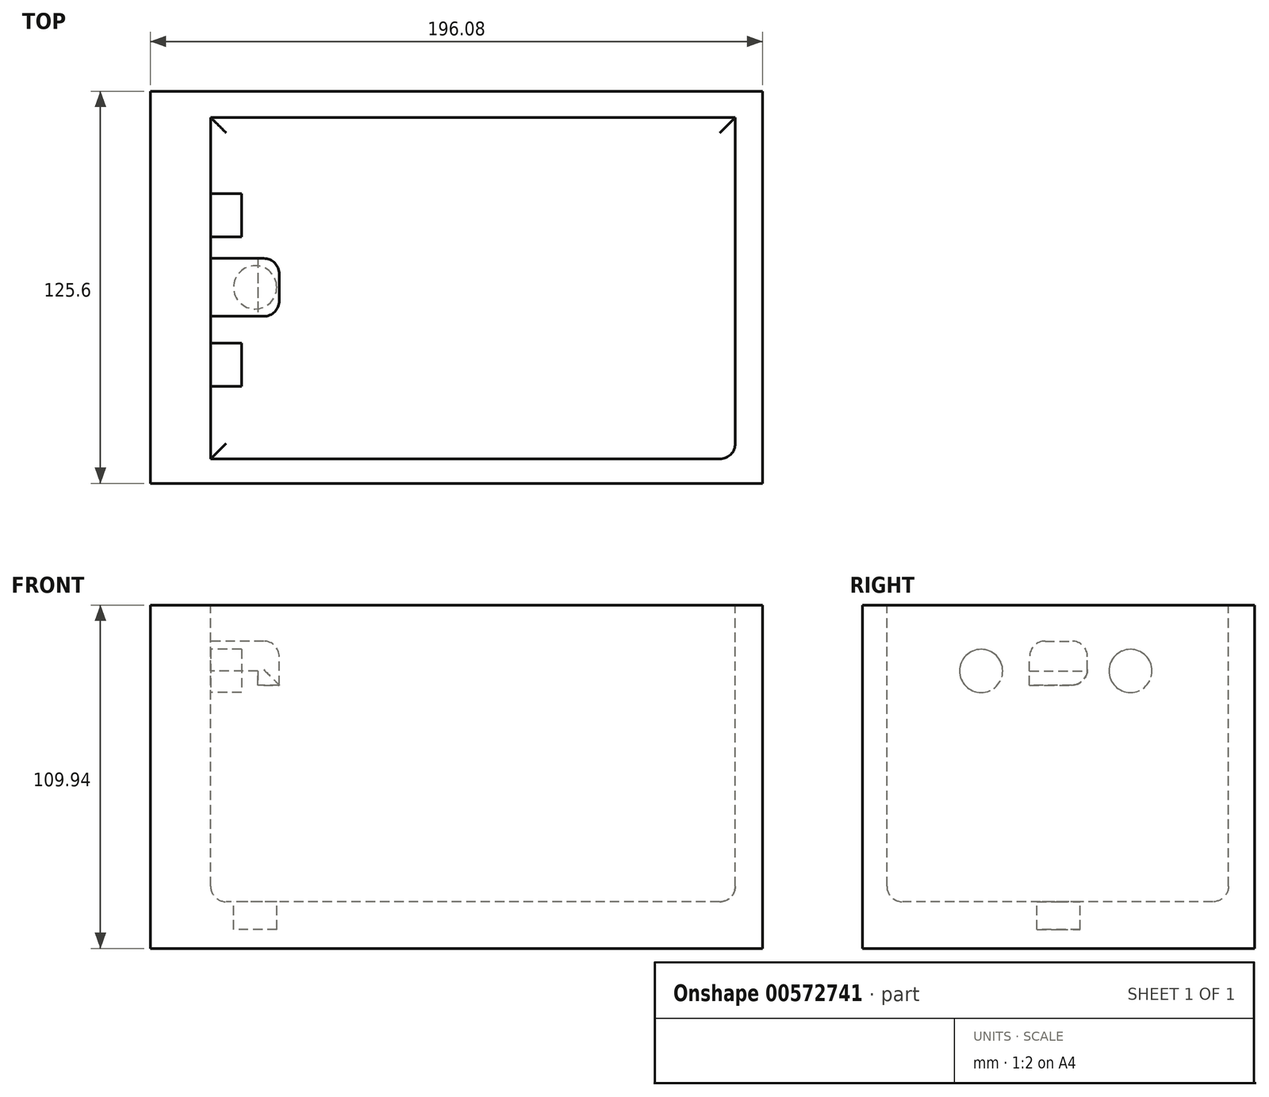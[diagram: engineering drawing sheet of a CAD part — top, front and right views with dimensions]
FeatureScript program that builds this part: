
annotation { "Feature Type Name" : "Feature", "Feature Type Description" : "" }
export const myFeature = defineFeature(function(context is Context, id is Id, definition is map)
    precondition{}
    {
        {
            var Q0;
            Q0=qCreatedBy(makeId("Front.planeOp"),FACE);
            var sketch = newSketch(context, id + "F0", { "sketchPlane" : qUnion([Q0])});
            skLineSegment(sketch, "E0.bottom", {"start": v(98.04, 54.97) * mm, "end": v(-98.04, 54.97) * mm});
            skLineSegment(sketch, "E0.top", {"start": v(98.04, -54.97) * mm, "end": v(-98.04, -54.97) * mm});
            skLineSegment(sketch, "E0.left", {"start": v(98.04, 54.97) * mm, "end": v(98.04, -54.97) * mm});
            skLineSegment(sketch, "E0.right", {"start": v(-98.04, 54.97) * mm, "end": v(-98.04, -54.97) * mm});
            skPoint(sketch, "E0.middle", {"position": v(0, 0) * mm});
            skSolve(sketch);
        }
        {
            var Q0;
            Q0=makeQuery(id+"F0.imprint","IMPRINT",FACE,{"disambiguationData":[TD([[makeQuery(id+"F0.imprint","IMPRINT",EDGE,{"derivedFrom":sQuery(id+"F0.wireOp",EDGE,"E0.bottom")}),1.0]])]});
            extrude(context, id + "F1", {"entities" : qUnion([Q0]), "endBound" : BoundingType.SYMMETRIC, "depth" : 125.6 * mm, "offsetDistance" : 25 * mm});
        }
        {
            var Q0;
            Q0=makeQuery(id+"F1.opExtrude","SWEPT_FACE",FACE,{"disambiguationData":[OSD([sQuery(id+"F0.wireOp",EDGE,"E0.bottom")])]});
            var sketch = newSketch(context, id + "F2", { "sketchPlane" : qUnion([Q0])});
            skLineSegment(sketch, "E1.bottom", {"start": v(89.32, 54.44) * mm, "end": v(-78.75, 54.44) * mm});
            skLineSegment(sketch, "E1.top", {"start": v(89.32, -54.97) * mm, "end": v(-78.75, -54.97) * mm});
            skLineSegment(sketch, "E1.left", {"start": v(89.32, 54.44) * mm, "end": v(89.32, -54.97) * mm});
            skLineSegment(sketch, "E1.right", {"start": v(-78.75, 54.44) * mm, "end": v(-78.75, -54.97) * mm});
            skSolve(sketch);
        }
        {
            var Q0;
            Q0=makeQuery(id+"F2.imprint","IMPRINT",FACE,{"disambiguationData":[TD([[makeQuery(id+"F2.imprint","IMPRINT",EDGE,{"derivedFrom":sQuery(id+"F2.wireOp",EDGE,"E1.bottom")}),1.0]])]});
            extrude(context, id + "F3", {"entities" : qUnion([Q0]), "operationType" : NewBodyOperationType.REMOVE, "oppositeDirection" : true, "depth" : 95 * mm, "offsetDistance" : 25 * mm});
        }
        {
            var Q0;
            Q0=makeQuery(id+"F3.boolean.opBoolean","COPY",FACE,{"derivedFrom":makeQuery(id+"F3.opExtrude","CAP_FACE",FACE,{"disambiguationData":[OSD([sQuery(id+"F2.wireOp",EDGE,"E1.bottom"),sQuery(id+"F2.wireOp",EDGE,"E1.top"),sQuery(id+"F2.wireOp",EDGE,"E1.left"),sQuery(id+"F2.wireOp",EDGE,"E1.right")])],"isStart":false})});
            var sketch = newSketch(context, id + "F4", { "sketchPlane" : qUnion([Q0])});
            skCircle(sketch, "E2", {"center": v(-64.48, 0) * mm, "radius": 6.92 * mm});
            skSolve(sketch);
        }
        {
            var Q0;
            Q0=makeQuery(id+"F4.imprint","IMPRINT",FACE,{"disambiguationData":[TD([[makeQuery(id+"F4.imprint","IMPRINT",EDGE,{"derivedFrom":sQuery(id+"F4.wireOp",EDGE,"E2")}),1.0]])]});
            extrude(context, id + "F5", {"entities" : qUnion([Q0]), "operationType" : NewBodyOperationType.REMOVE, "oppositeDirection" : true, "depth" : 8.9 * mm, "offsetDistance" : 25 * mm});
        }
        {
            var Q0;
            Q0=makeQuery(id+"F3.boolean.opBoolean","COPY",FACE,{"derivedFrom":makeQuery(id+"F3.opExtrude","SWEPT_FACE",FACE,{"disambiguationData":[OSD([sQuery(id+"F2.wireOp",EDGE,"E1.right")])]})});
            var sketch = newSketch(context, id + "F6", { "sketchPlane" : qUnion([Q0])});
            skLineSegment(sketch, "E3.bottom", {"start": v(-9.27, 33.92) * mm, "end": v(9.27, 33.92) * mm});
            skLineSegment(sketch, "E3.top", {"start": v(-9.27, 43.45) * mm, "end": v(9.27, 43.45) * mm});
            skLineSegment(sketch, "E3.left", {"start": v(-9.27, 33.92) * mm, "end": v(-9.27, 43.45) * mm});
            skLineSegment(sketch, "E3.right", {"start": v(9.27, 33.92) * mm, "end": v(9.27, 43.45) * mm});
            skPoint(sketch, "E3.middle", {"position": v(0, 38.69) * mm});
            skSolve(sketch);
        }
        {
            var Q0;
            Q0=makeQuery(id+"F6.imprint","IMPRINT",FACE,{"disambiguationData":[TD([[makeQuery(id+"F6.imprint","IMPRINT",EDGE,{"derivedFrom":sQuery(id+"F6.wireOp",EDGE,"E3.bottom")}),1.0]])]});
            extrude(context, id + "F7", {"entities" : qUnion([Q0]), "operationType" : NewBodyOperationType.ADD, "depth" : 22 * mm, "offsetDistance" : 25 * mm});
        }
        {
            var Q0;
            Q0=makeQuery(id+"F7.opExtrude","SWEPT_FACE",FACE,{"disambiguationData":[OSD([sQuery(id+"F6.wireOp",EDGE,"E3.top")])]});
            var sketch = newSketch(context, id + "F8", { "sketchPlane" : qUnion([Q0])});
            skLineSegment(sketch, "E4.bottom", {"start": v(-56.75, 9.27) * mm, "end": v(-63.69, 9.27) * mm});
            skLineSegment(sketch, "E4.top", {"start": v(-56.75, -9.27) * mm, "end": v(-63.69, -9.27) * mm});
            skLineSegment(sketch, "E4.left", {"start": v(-56.75, 9.27) * mm, "end": v(-56.75, -9.27) * mm});
            skLineSegment(sketch, "E4.right", {"start": v(-63.69, 9.27) * mm, "end": v(-63.69, -9.27) * mm});
            skSolve(sketch);
        }
        {
            var Q0;
            Q0=makeQuery(id+"F8.imprint","IMPRINT",FACE,{"disambiguationData":[TD([[makeQuery(id+"F8.imprint","IMPRINT",EDGE,{"derivedFrom":sQuery(id+"F8.wireOp",EDGE,"E4.bottom")}),1.0]])]});
            extrude(context, id + "F9", {"entities" : qUnion([Q0]), "operationType" : NewBodyOperationType.ADD, "oppositeDirection" : true, "depth" : 14.1 * mm, "offsetDistance" : 25 * mm});
        }
        {
            var Q0;
            Q0=makeQuery(id+"F3.boolean.opBoolean","COPY",EDGE,{"derivedFrom":makeQuery(id+"F3.opExtrude","CAP_EDGE",EDGE,{"disambiguationData":[OSD([sQuery(id+"F2.wireOp",EDGE,"E1.top")])],"isStart":true})});
            var Q1;
            Q1=makeQuery(id+"F3.boolean.opBoolean","COPY",EDGE,{"derivedFrom":makeQuery(id+"F3.opExtrude","SWEPT_EDGE",EDGE,{"disambiguationData":[OSD([sQuery(id+"F2.wireOp",EDGE,"E1.top"),sQuery(id+"F2.wireOp",EDGE,"E1.left")])]})});
            var Q2;
            Q2=makeQuery(id+"F3.boolean.opBoolean","COPY",EDGE,{"derivedFrom":makeQuery(id+"F3.opExtrude","CAP_EDGE",EDGE,{"disambiguationData":[OSD([sQuery(id+"F2.wireOp",EDGE,"E1.top")])],"isStart":false})});
            var Q3;
            Q3=makeQuery(id+"F7.opExtrude","SWEPT_EDGE",EDGE,{"disambiguationData":[OSD([sQuery(id+"F6.wireOp",EDGE,"E3.top"),sQuery(id+"F6.wireOp",EDGE,"E3.right")])]});
            var Q4;
            Q4=makeQuery(id+"F7.opExtrude","SWEPT_EDGE",EDGE,{"disambiguationData":[OSD([sQuery(id+"F6.wireOp",EDGE,"E3.top"),sQuery(id+"F6.wireOp",EDGE,"E3.left")])]});
            var Q5;
            Q5=makeQuery(id+"F7.opExtrude","CAP_EDGE",EDGE,{"disambiguationData":[OSD([sQuery(id+"F6.wireOp",EDGE,"E3.top")])],"isStart":false});
            var Q6;
            Q6=makeQuery(id+"F9.opExtrude","CAP_EDGE",EDGE,{"disambiguationData":[OSD([sQuery(id+"F8.wireOp",EDGE,"E4.bottom")])],"isStart":false});
            var Q7;
            Q7=makeQuery(id+"F9.boolean.opBoolean","MERGE",EDGE,{"derivedFrom":[makeQuery(id+"F7.opExtrude","CAP_EDGE",EDGE,{"disambiguationData":[OSD([sQuery(id+"F6.wireOp",EDGE,"E3.left")])],"isStart":false}),makeQuery(id+"F9.opExtrude","SWEPT_EDGE",EDGE,{"disambiguationData":[OSD([sQuery(id+"F8.wireOp",EDGE,"E4.top"),sQuery(id+"F8.wireOp",EDGE,"E4.left")])]})]});
            var Q8;
            Q8=makeQuery(id+"F3.boolean.opBoolean","COPY",EDGE,{"derivedFrom":makeQuery(id+"F3.opExtrude","CAP_EDGE",EDGE,{"disambiguationData":[OSD([sQuery(id+"F2.wireOp",EDGE,"E1.right")])],"isStart":true})});
            var Q9;
            Q9=makeQuery(id+"F3.boolean.opBoolean","COPY",EDGE,{"derivedFrom":makeQuery(id+"F3.opExtrude","CAP_EDGE",EDGE,{"disambiguationData":[OSD([sQuery(id+"F2.wireOp",EDGE,"E1.bottom")])],"isStart":true})});
            var Q10;
            Q10=makeQuery(id+"F3.boolean.opBoolean","COPY",EDGE,{"derivedFrom":makeQuery(id+"F3.opExtrude","CAP_EDGE",EDGE,{"disambiguationData":[OSD([sQuery(id+"F2.wireOp",EDGE,"E1.right")])],"isStart":false})});
            var Q11;
            Q11=makeQuery(id+"F3.boolean.opBoolean","COPY",EDGE,{"derivedFrom":makeQuery(id+"F3.opExtrude","CAP_EDGE",EDGE,{"disambiguationData":[OSD([sQuery(id+"F2.wireOp",EDGE,"E1.bottom")])],"isStart":false})});
            var Q12;
            Q12=makeQuery(id+"F3.boolean.opBoolean","COPY",EDGE,{"derivedFrom":makeQuery(id+"F3.opExtrude","CAP_EDGE",EDGE,{"disambiguationData":[OSD([sQuery(id+"F2.wireOp",EDGE,"E1.left")])],"isStart":false})});
            var Q13;
            Q13=makeQuery(id+"F9.boolean.opBoolean","MERGE",EDGE,{"derivedFrom":[makeQuery(id+"F7.opExtrude","CAP_EDGE",EDGE,{"disambiguationData":[OSD([sQuery(id+"F6.wireOp",EDGE,"E3.right")])],"isStart":false}),makeQuery(id+"F9.opExtrude","SWEPT_EDGE",EDGE,{"disambiguationData":[OSD([sQuery(id+"F8.wireOp",EDGE,"E4.bottom"),sQuery(id+"F8.wireOp",EDGE,"E4.left")])]})]});
            fillet(context, id + "F10", {"entities" : qUnion([Q0, Q1, Q2, Q3, Q4, Q5, Q6, Q7, Q8, Q9, Q10, Q11, Q12, Q13]), "radius" : 5 * mm, "tangentPropagation" : true, "allowEdgeOverflow" : false});
        }
        {
            var Q0;
            Q0=makeQuery(id+"F3.boolean.opBoolean","COPY",FACE,{"derivedFrom":makeQuery(id+"F3.opExtrude","SWEPT_FACE",FACE,{"disambiguationData":[OSD([sQuery(id+"F2.wireOp",EDGE,"E1.right")])]})});
            var sketch = newSketch(context, id + "F11", { "sketchPlane" : qUnion([Q0])});
            skCircle(sketch, "E5", {"center": v(23.06, 33.92) * mm, "radius": 6.9 * mm});
            skCircle(sketch, "E6", {"center": v(-24.77, 33.92) * mm, "radius": 6.9 * mm});
            skSolve(sketch);
        }
        {
            var Q0;
            Q0=makeQuery(id+"F11.imprint","IMPRINT",FACE,{"disambiguationData":[TD([[makeQuery(id+"F11.imprint","IMPRINT",EDGE,{"derivedFrom":sQuery(id+"F11.wireOp",EDGE,"E6")}),1.0]])]});
            var Q1;
            Q1=makeQuery(id+"F11.imprint","IMPRINT",FACE,{"disambiguationData":[TD([[makeQuery(id+"F11.imprint","IMPRINT",EDGE,{"derivedFrom":sQuery(id+"F11.wireOp",EDGE,"E5")}),1.0]])]});
            extrude(context, id + "F12", {"entities" : qUnion([Q0, Q1]), "operationType" : NewBodyOperationType.ADD, "depth" : 9.9 * mm, "offsetDistance" : 25 * mm});
        }
    });
